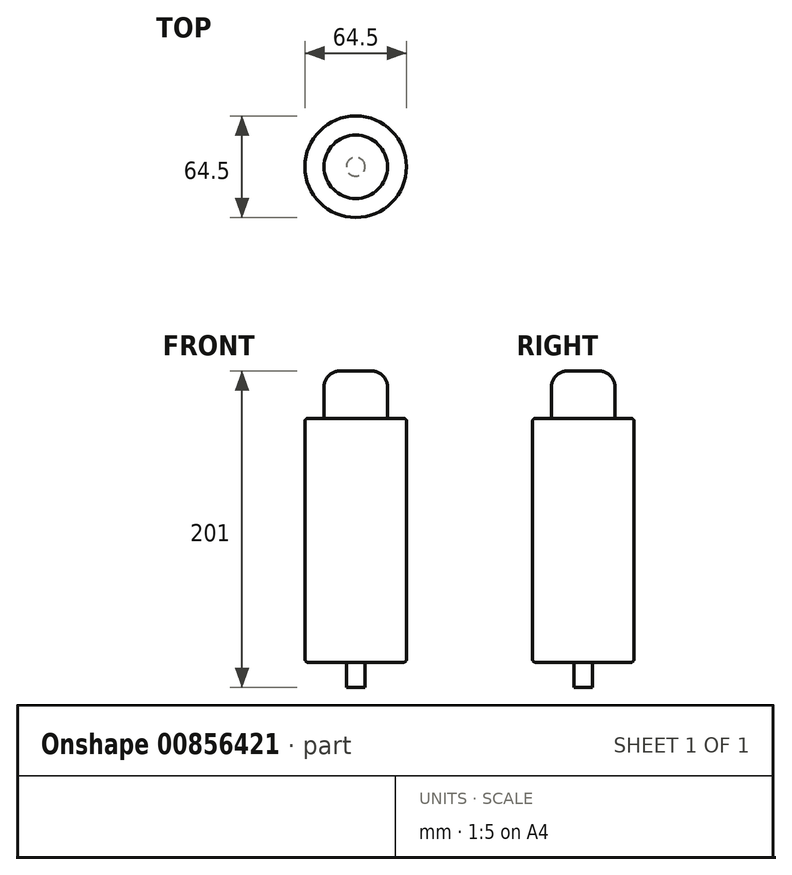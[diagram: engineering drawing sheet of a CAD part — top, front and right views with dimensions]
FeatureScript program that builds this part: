
annotation { "Feature Type Name" : "Feature", "Feature Type Description" : "" }
export const myFeature = defineFeature(function(context is Context, id is Id, definition is map)
    precondition{}
    {
        {
            var Q0;
            Q0=qCreatedBy(makeId("Top.planeOp"),FACE);
            var sketch = newSketch(context, id + "F0", { "sketchPlane" : qUnion([Q0])});
            skCircle(sketch, "E0", {"center": v(0, 0) * mm, "radius": 32.25 * mm});
            skSolve(sketch);
        }
        {
            var Q0;
            Q0 = qSketchRegion(id + "F0", true);
            extrude(context, id + "F1", {"entities" : qUnion([Q0]), "depth" : 155 * mm, "offsetDistance" : 25 * mm});
        }
        {
            var Q0;
            Q0=makeQuery(id+"F1.opExtrude","CAP_FACE",FACE,{"disambiguationData":[OSD([sQuery(id+"F0.wireOp",EDGE,"E0")])],"isStart":false});
            var sketch = newSketch(context, id + "F2", { "sketchPlane" : qUnion([Q0])});
            skCircle(sketch, "E1", {"center": v(0, 0) * mm, "radius": 20.14 * mm});
            skSolve(sketch);
        }
        {
            var Q0;
            Q0=makeQuery(id+"F2.imprint","IMPRINT",FACE,{"disambiguationData":[TD([[makeQuery(id+"F2.imprint","IMPRINT",EDGE,{"derivedFrom":sQuery(id+"F2.wireOp",EDGE,"E1")}),1.0]])]});
            extrude(context, id + "F3", {"entities" : qUnion([Q0]), "operationType" : NewBodyOperationType.ADD, "depth" : 30 * mm, "offsetDistance" : 25 * mm});
        }
        {
            var Q0;
            Q0=makeQuery(id+"F3.opExtrude","CAP_EDGE",EDGE,{"disambiguationData":[OSD([sQuery(id+"F2.wireOp",EDGE,"E1")])],"isStart":false});
            fillet(context, id + "F4", {"entities" : qUnion([Q0]), "radius" : 10 * mm, "tangentPropagation" : true, "allowEdgeOverflow" : false});
        }
        {
            var Q0;
            Q0=makeQuery(id+"F1.opExtrude","CAP_FACE",FACE,{"disambiguationData":[OSD([sQuery(id+"F0.wireOp",EDGE,"E0")])],"isStart":true});
            var sketch = newSketch(context, id + "F5", { "sketchPlane" : qUnion([Q0])});
            skCircle(sketch, "E2", {"center": v(0, 0) * mm, "radius": 6 * mm});
            skSolve(sketch);
        }
        {
            var Q0;
            Q0=makeQuery(id+"F5.imprint","IMPRINT",FACE,{"disambiguationData":[TD([[makeQuery(id+"F5.imprint","IMPRINT",EDGE,{"derivedFrom":sQuery(id+"F5.wireOp",EDGE,"E2")}),1.0]])]});
            extrude(context, id + "F6", {"entities" : qUnion([Q0]), "operationType" : NewBodyOperationType.ADD, "depth" : 16 * mm, "offsetDistance" : 25 * mm});
        }
        {
            var Q0;
            Q0=makeQuery(id+"F1.opExtrude","CAP_EDGE",EDGE,{"disambiguationData":[OSD([sQuery(id+"F0.wireOp",EDGE,"E0")])],"isStart":false});
            var Q1;
            Q1=makeQuery(id+"F1.opExtrude","CAP_EDGE",EDGE,{"disambiguationData":[OSD([sQuery(id+"F0.wireOp",EDGE,"E0")])],"isStart":true});
            fillet(context, id + "F7", {"entities" : qUnion([Q0, Q1]), "radius" : 2 * mm, "tangentPropagation" : true, "allowEdgeOverflow" : false});
        }
    });
